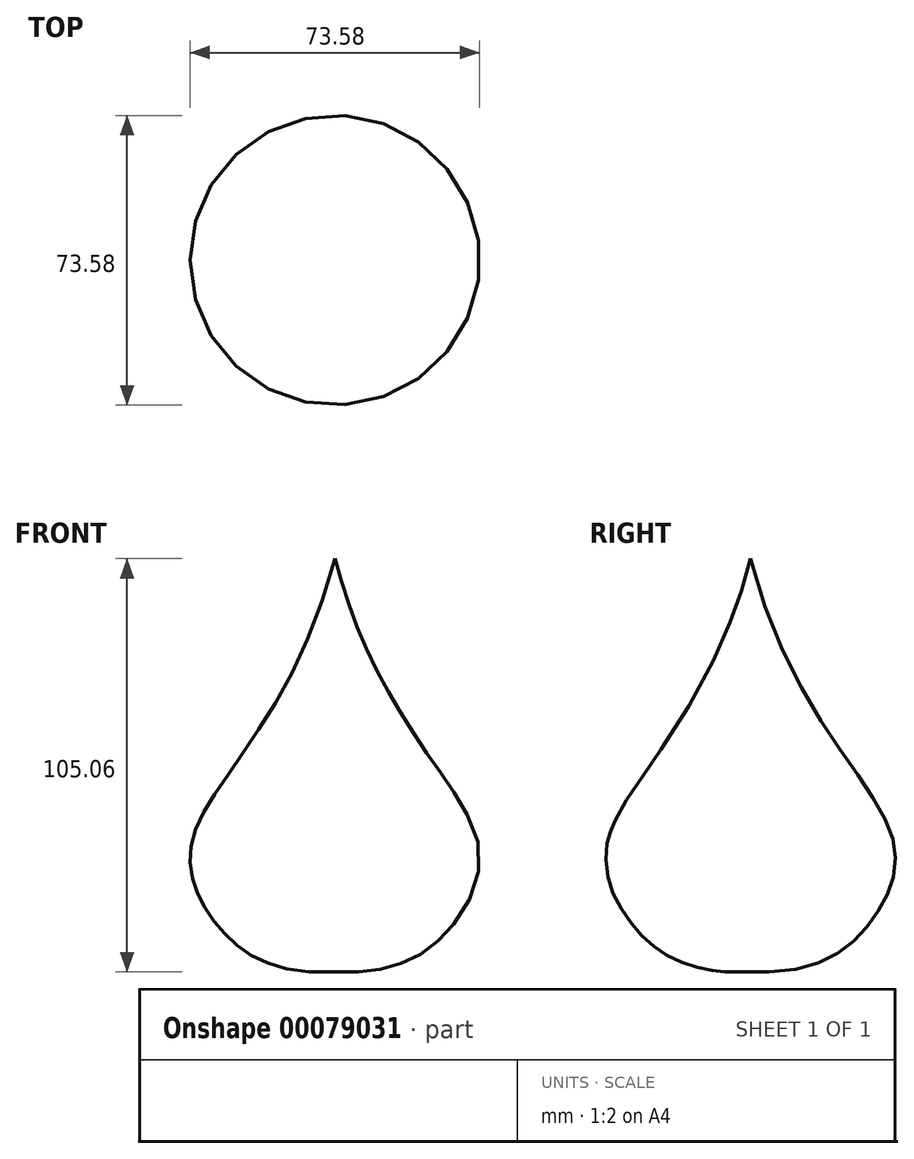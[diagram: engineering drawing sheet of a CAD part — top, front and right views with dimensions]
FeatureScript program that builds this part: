
annotation { "Feature Type Name" : "Feature", "Feature Type Description" : "" }
export const myFeature = defineFeature(function(context is Context, id is Id, definition is map)
    precondition{}
    {
        {
            var Q0;
            Q0=qCreatedBy(makeId("Front.planeOp"),FACE);
            var sketch = newSketch(context, id + "F0", { "sketchPlane" : qUnion([Q0])});
            skFitSpline(sketch, "E0", {"points": [v(0, 69.35) * mm, v(-36.23, -2.2) * mm, v(-30, -23.7) * mm, v(0, -35.62) * mm], "startDerivative": vector(-67.54, -263.12) * mm, "endDerivative": vector(162.13, 8.83) * mm});
            skLineSegment(sketch, "E1", {"start": v(0, 69.35) * mm, "end": v(0, -35.62) * mm});
            skFitSpline(sketch, "E2.0", {"points": [v(-1.94, 69.84) * mm, v(-3.33, 64.44) * mm, v(-6.52, 54.5) * mm, v(-12.15, 41.93) * mm, v(-18.16, 31.3) * mm, v(-24.14, 22.25) * mm, v(-28.75, 15.74) * mm, v(-32, 10.95) * mm, v(-34.16, 7.52) * mm, v(-36, 4.19) * mm, v(-37.2, 1.45) * mm, v(-37.93, -0.75) * mm, v(-38.49, -2.96) * mm, v(-38.84, -5.7) * mm, v(-38.76, -8.94) * mm, v(-38.06, -13.14) * mm, v(-36.58, -17.1) * mm, v(-34.53, -20.8) * mm, v(-33.06, -23) * mm, v(-31.79, -24.68) * mm, v(-30.46, -26.3) * mm, v(-28.67, -28.27) * mm, v(-26.28, -30.46) * mm, v(-22.7, -33.09) * mm, v(-17.45, -35.74) * mm, v(-9.68, -37.6) * mm, v(-3.37, -37.8) * mm, v(0.1, -37.62) * mm]});
            skLineSegment(sketch, "E3", {"start": v(0, 69.35) * mm, "end": v(-2.1, 69.23) * mm});
            skLineSegment(sketch, "E4", {"start": v(0.1, -37.62) * mm, "end": v(0, -35.62) * mm});
            skSolve(sketch);
        }
        {
            var Q0;
            Q0=makeQuery(id+"F0.imprint","IMPRINT",FACE,{"disambiguationData":[TD([[makeQuery(id+"F0.imprint","IMPRINT",EDGE,{"derivedFrom":sQuery(id+"F0.wireOp",EDGE,"E0")}),1.0]])]});
            var Q1;
            Q1=sQuery(id+"F0.wireOp",EDGE,"E1");
            revolve(context, id + "F1", {"entities" : qUnion([Q0]), "axis" : qUnion([Q1]), "revolveType" : RevolveType.FULL});
        }
    });
